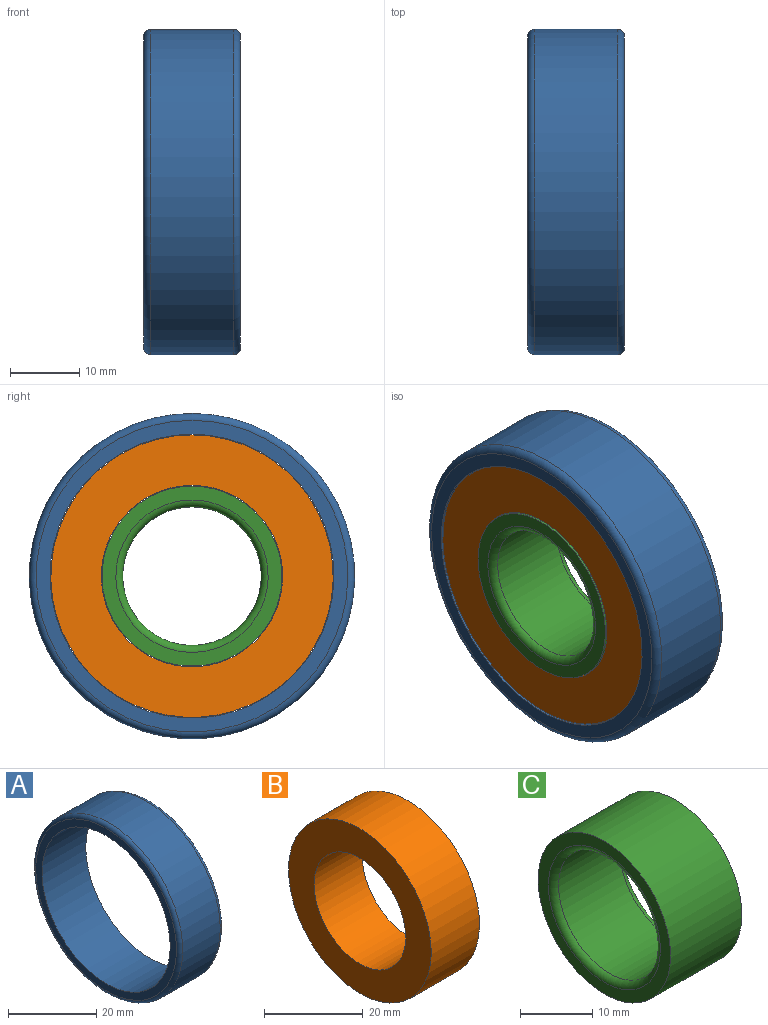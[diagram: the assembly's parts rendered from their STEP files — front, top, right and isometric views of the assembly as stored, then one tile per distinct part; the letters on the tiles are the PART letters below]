
ASSEMBLY  parts=3 mates=2
PART A: 6 faces, bbox 14x50.9x50.9 mm
  f0: torus R=22.5mm, axis (-1,0,0), area 228.3mm2, adj f1,f5
  f1: plane 45x45mm, normal (-1,0,0), area 270.2mm2, adj f0,f2
  f2: cylinder r=20.5mm len=41mm, axis (-1,0,0), area 1803.3mm2, adj f1,f3
  f3: plane 45x45mm, normal (1,0,0), area 270.2mm2, adj f2,f4
  f4: torus R=22.5mm, axis (-1,0,0), area 228.3mm2, adj f3,f5
  f5: cylinder r=23.5mm len=47mm, axis (-1,0,0), area 1771.9mm2, adj f0,f4
PART B: 4 faces, bbox 13.8x40.8x40.8 mm
  f0: cylinder r=20.4mm len=40.8mm, axis (-1,0,0), area 1768.8mm2, adj f1,f3
  f1: plane 40.8x40.8mm, normal (-1,0,0), area 768.3mm2, adj f0,f2
  f2: cylinder r=13.1mm len=26.2mm, axis (-1,0,0), area 1135.9mm2, adj f1,f3
  f3: plane 40.8x40.8mm, normal (1,0,0), area 768.3mm2, adj f0,f2
PART C: 6 faces, bbox 14x26x26 mm
  f0: plane 26x26mm, normal (1,0,0), area 150.8mm2, adj f1,f5
  f1: cylinder r=13mm len=26mm, axis (-1,0,0), area 1143.5mm2, adj f0,f2
  f2: plane 26x26mm, normal (-1,0,0), area 150.8mm2, adj f1,f3
  f3: torus R=11mm, axis (-1,0,0), area 102.3mm2, adj f2,f4
  f4: cylinder r=10mm len=20mm, axis (-1,0,0), area 754mm2, adj f3,f5
  f5: torus R=11mm, axis (-1,0,0), area 102.3mm2, adj f0,f4
PLACE A t=(10.39,66.6,30.28)mm
PLACE B t=(10.49,66.6,30.28)mm
PLACE C t=(10.39,66.6,30.28)mm
MATE revolute B.f0 <-> C.f1  axis (1,0,0) through (24.39,66.6,30.28)mm
MATE revolute C.f1 <-> A.f0  axis (1,0,0) through (24.39,66.6,30.28)mm
